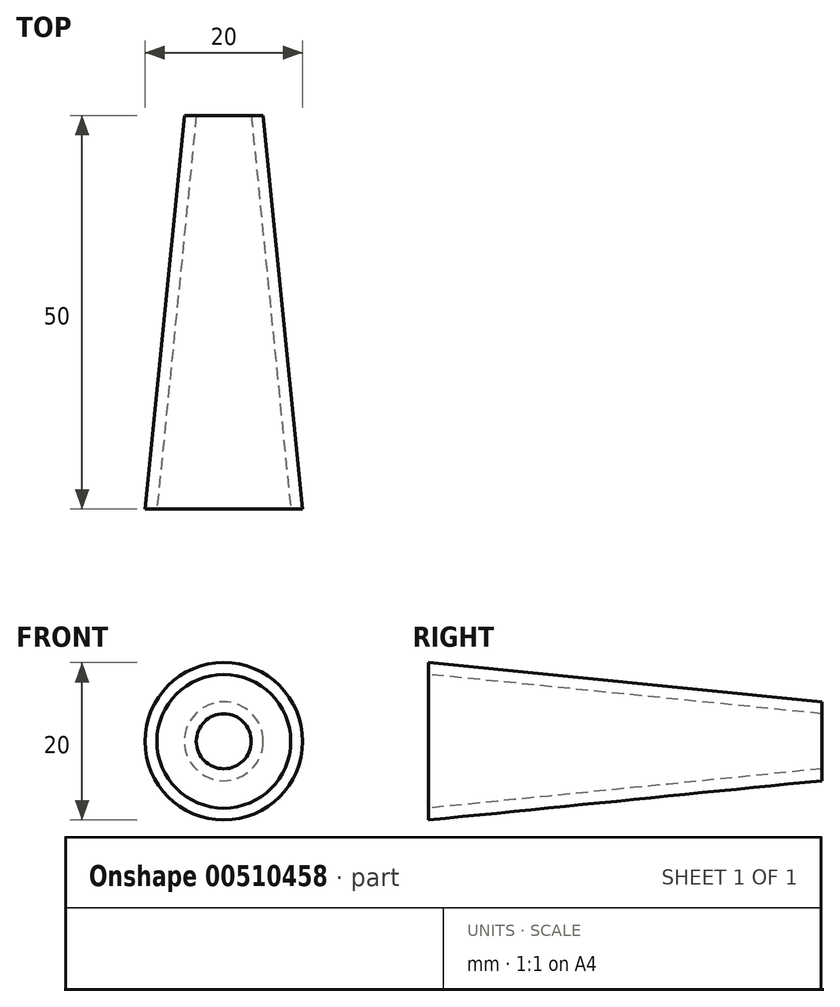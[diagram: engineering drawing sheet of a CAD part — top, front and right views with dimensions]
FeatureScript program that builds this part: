
annotation { "Feature Type Name" : "Feature", "Feature Type Description" : "" }
export const myFeature = defineFeature(function(context is Context, id is Id, definition is map)
    precondition{}
    {
        {
            var Q0;
            Q0=qCreatedBy(makeId("Front.planeOp"),FACE);
            var sketch = newSketch(context, id + "F0", { "sketchPlane" : qUnion([Q0])});
            skCircle(sketch, "E0", {"center": v(0, 0) * mm, "radius": 10 * mm});
            skSolve(sketch);
        }
        {
            var Q0;
            Q0=makeQuery(id+"F0.imprint","IMPRINT",FACE,{"disambiguationData":[TD([[makeQuery(id+"F0.imprint","IMPRINT",EDGE,{"derivedFrom":sQuery(id+"F0.wireOp",EDGE,"E0")}),1.0]])]});
            extrude(context, id + "F1", {"entities" : qUnion([Q0]), "depth" : 25 * mm});
        }
        {
            var Q0;
            Q0=makeQuery(id+"F1.opExtrude","CAP_FACE",FACE,{"disambiguationData":[OSD([sQuery(id+"F0.wireOp",EDGE,"E0")])],"isStart":true});
            extrude(context, id + "F2", {"entities" : qUnion([Q0]), "operationType" : NewBodyOperationType.ADD, "depth" : 25 * mm});
        }
        {
            var Q0;
            Q0=makeQuery(id+"F2.opExtrude","CAP_FACE",FACE,{"disambiguationData":[OSD([sQuery(id+"F0.wireOp",EDGE,"E0")])],"isStart":false});
            var sketch = newSketch(context, id + "F3", { "sketchPlane" : qUnion([Q0])});
            skCircle(sketch, "E1", {"center": v(0, 0) * mm, "radius": 5 * mm});
            skSolve(sketch);
        }
        {
            var Q1;
            Q1=makeQuery(id+"F3.imprint","IMPRINT",FACE,{"disambiguationData":[TD([[makeQuery(id+"F3.imprint","IMPRINT",EDGE,{"derivedFrom":sQuery(id+"F3.wireOp",EDGE,"E1")}),1.0]])]});
            var Q2;
            Q2=makeQuery(id+"F1.opExtrude","CAP_FACE",FACE,{"disambiguationData":[OSD([sQuery(id+"F0.wireOp",EDGE,"E0")])],"isStart":false});
            loft(context, id + "F4", {"operationType" : NewBodyOperationType.INTERSECT, "sheetProfilesArray" : [{ "sheetProfileEntities" : qUnion([Q1]) }, { "sheetProfileEntities" : qUnion([Q2]) }]});
        }
        {
            var Q0;
            Q0=makeQuery(id+"F1.opExtrude","CAP_FACE",FACE,{"disambiguationData":[OSD([sQuery(id+"F0.wireOp",EDGE,"E0")])],"isStart":false});
            var Q1;
            Q1=makeQuery(id+"F2.opExtrude","CAP_FACE",FACE,{"disambiguationData":[OSD([sQuery(id+"F0.wireOp",EDGE,"E0")])],"isStart":false});
            shell(context, id + "F5", {"entities" : qUnion([Q0, Q1]), "thickness" : 1.5 * mm});
        }
    });
